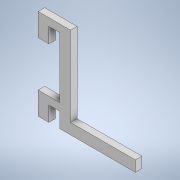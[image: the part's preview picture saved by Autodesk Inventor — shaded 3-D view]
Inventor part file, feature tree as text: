
AUTODESK INVENTOR PART (.ipt)
format: ipt  version: 2020.2 (Build 242310000, 310)  size: 124,416 bytes
history: native  units: in
note: dims shown in document units (in); Inventor stores cm internally (conversion verified against a paired STEP export)
features: extrude x1, sketch x1
ambient origin geometry x8: Origin, YZ Plane, XZ Plane, XY Plane, X Axis, Y Axis, Z Axis, Center Point
bodies: Solid1 (feature_tree)
feature tree (2):
  extrude  "Extrusion1"  Depth=0.175in
  sketch  "Sketch1"  dims[d1=1.4in d2=0.175in d3=0.175in d4=0.25in d6=0.25in d7=0.25in d10=1.5in d11=0.15in d12=0.0in d13=0.525in d14=0.525in]
